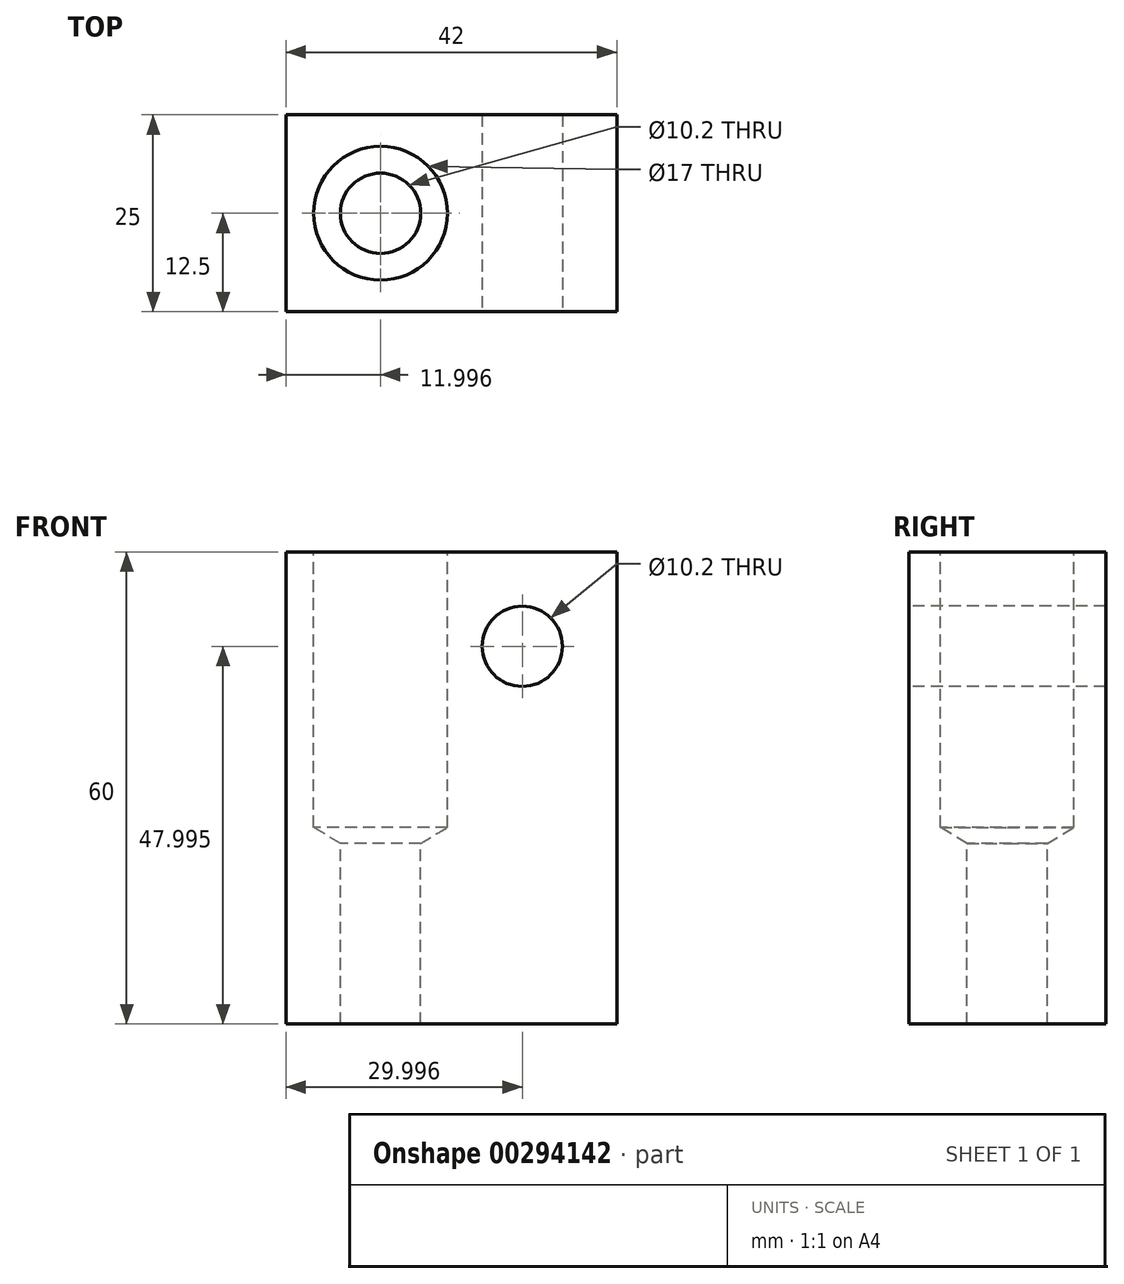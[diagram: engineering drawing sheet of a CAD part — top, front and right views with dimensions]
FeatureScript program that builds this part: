
annotation { "Feature Type Name" : "Feature", "Feature Type Description" : "" }
export const myFeature = defineFeature(function(context is Context, id is Id, definition is map)
    precondition{}
    {
        {
            var Q0;
            Q0=qCreatedBy(makeId("Front.planeOp"),FACE);
            var sketch = newSketch(context, id + "F0", { "sketchPlane" : qUnion([Q0])});
            skLineSegment(sketch, "E0.bottom", {"start": v(-73.57, 78.06) * mm, "end": v(-31.57, 78.06) * mm});
            skLineSegment(sketch, "E0.top", {"start": v(-73.57, 18.06) * mm, "end": v(-31.57, 18.06) * mm});
            skLineSegment(sketch, "E0.left", {"start": v(-73.57, 78.06) * mm, "end": v(-73.57, 18.06) * mm});
            skLineSegment(sketch, "E0.right", {"start": v(-31.57, 78.06) * mm, "end": v(-31.57, 18.06) * mm});
            skSolve(sketch);
        }
        {
            var Q0;
            Q0=makeQuery(id+"F0.imprint","IMPRINT",FACE,{"disambiguationData":[TD([[makeQuery(id+"F0.imprint","IMPRINT",EDGE,{"derivedFrom":sQuery(id+"F0.wireOp",EDGE,"E0.bottom")}),-1.0]])]});
            extrude(context, id + "F1", {"entities" : qUnion([Q0]), "depth" : 25 * mm});
        }
        {
            var Q0;
            Q0=makeQuery(id+"F1.opExtrude","SWEPT_FACE",FACE,{"disambiguationData":[OSD([sQuery(id+"F0.wireOp",EDGE,"E0.bottom")])]});
            var sketch = newSketch(context, id + "F2", { "sketchPlane" : qUnion([Q0])});
            skLineSegment(sketch, "E1", {"start": v(-73.57, 0) * mm, "end": v(-73.57, -12.5) * mm});
            skLineSegment(sketch, "E2", {"start": v(-70.32, -12.5) * mm, "end": v(-61.57, -12.5) * mm});
            skCircle(sketch, "E3", {"center": v(-61.57, -12.5) * mm, "radius": 8.75 * mm});
            skCircle(sketch, "E4", {"center": v(-61.57, -12.5) * mm, "radius": 5.1 * mm});
            skSolve(sketch);
        }
        {
            var Q0;
            Q0=makeQuery(id+"F1.opExtrude","CAP_FACE",FACE,{"disambiguationData":[OSD([sQuery(id+"F0.wireOp",EDGE,"E0.bottom"),sQuery(id+"F0.wireOp",EDGE,"E0.top"),sQuery(id+"F0.wireOp",EDGE,"E0.left"),sQuery(id+"F0.wireOp",EDGE,"E0.right")])],"isStart":false});
            var sketch = newSketch(context, id + "F3", { "sketchPlane" : qUnion([Q0])});
            skLineSegment(sketch, "E5", {"start": v(-31.57, 78.06) * mm, "end": v(-43.57, 78.06) * mm});
            skCircle(sketch, "E6", {"center": v(-43.57, 66.06) * mm, "radius": 5.1 * mm});
            skSolve(sketch);
        }
        {
            var Q0;
            Q0=sQuery(id+"F3.wireOp",VERTEX,"E6.center");
            var Q1;
            Q1=makeQuery(id+"F1.opExtrude","SWEPT_BODY",BODY,{"disambiguationData":[OSD([sQuery(id+"F0.wireOp",EDGE,"E0.bottom"),sQuery(id+"F0.wireOp",EDGE,"E0.top"),sQuery(id+"F0.wireOp",EDGE,"E0.left"),sQuery(id+"F0.wireOp",EDGE,"E0.right")])]});
            hole(context, id + "F4", {"style" : HoleStyle.SIMPLE, "endStyle" : HoleEndStyle.BLIND, "holeDiameter" : 10.2 * mm, "holeDepth" : 100 * mm, "tappedDepth" : 12 * mm, "tapClearance" : 3, "startFromSketch" : true, "locations" : qUnion([Q0]), "scope" : qUnion([Q1])});
        }
        {
            var Q0;
            Q0=sQuery(id+"F2.wireOp",VERTEX,"E2.end");
            var Q1;
            Q1=makeQuery(id+"F1.opExtrude","SWEPT_BODY",BODY,{"disambiguationData":[OSD([sQuery(id+"F0.wireOp",EDGE,"E0.bottom"),sQuery(id+"F0.wireOp",EDGE,"E0.top"),sQuery(id+"F0.wireOp",EDGE,"E0.left"),sQuery(id+"F0.wireOp",EDGE,"E0.right")])]});
            hole(context, id + "F5", {"style" : HoleStyle.SIMPLE, "endStyle" : HoleEndStyle.BLIND, "holeDiameter" : 10.2 * mm, "holeDepth" : 100 * mm, "tappedDepth" : 12 * mm, "tapClearance" : 3, "startFromSketch" : true, "locations" : qUnion([Q0]), "scope" : qUnion([Q1])});
        }
        {
            var Q0;
            Q0=sQuery(id+"F2.wireOp",VERTEX,"E4.center");
            var Q1;
            Q1=makeQuery(id+"F1.opExtrude","SWEPT_BODY",BODY,{"disambiguationData":[OSD([sQuery(id+"F0.wireOp",EDGE,"E0.bottom"),sQuery(id+"F0.wireOp",EDGE,"E0.top"),sQuery(id+"F0.wireOp",EDGE,"E0.left"),sQuery(id+"F0.wireOp",EDGE,"E0.right")])]});
            hole(context, id + "F6", {"style" : HoleStyle.SIMPLE, "endStyle" : HoleEndStyle.BLIND, "holeDiameter" : 17 * mm, "holeDepth" : 35 * mm, "tappedDepth" : 12 * mm, "tapClearance" : 3, "startFromSketch" : true, "locations" : qUnion([Q0]), "scope" : qUnion([Q1])});
        }
    });
